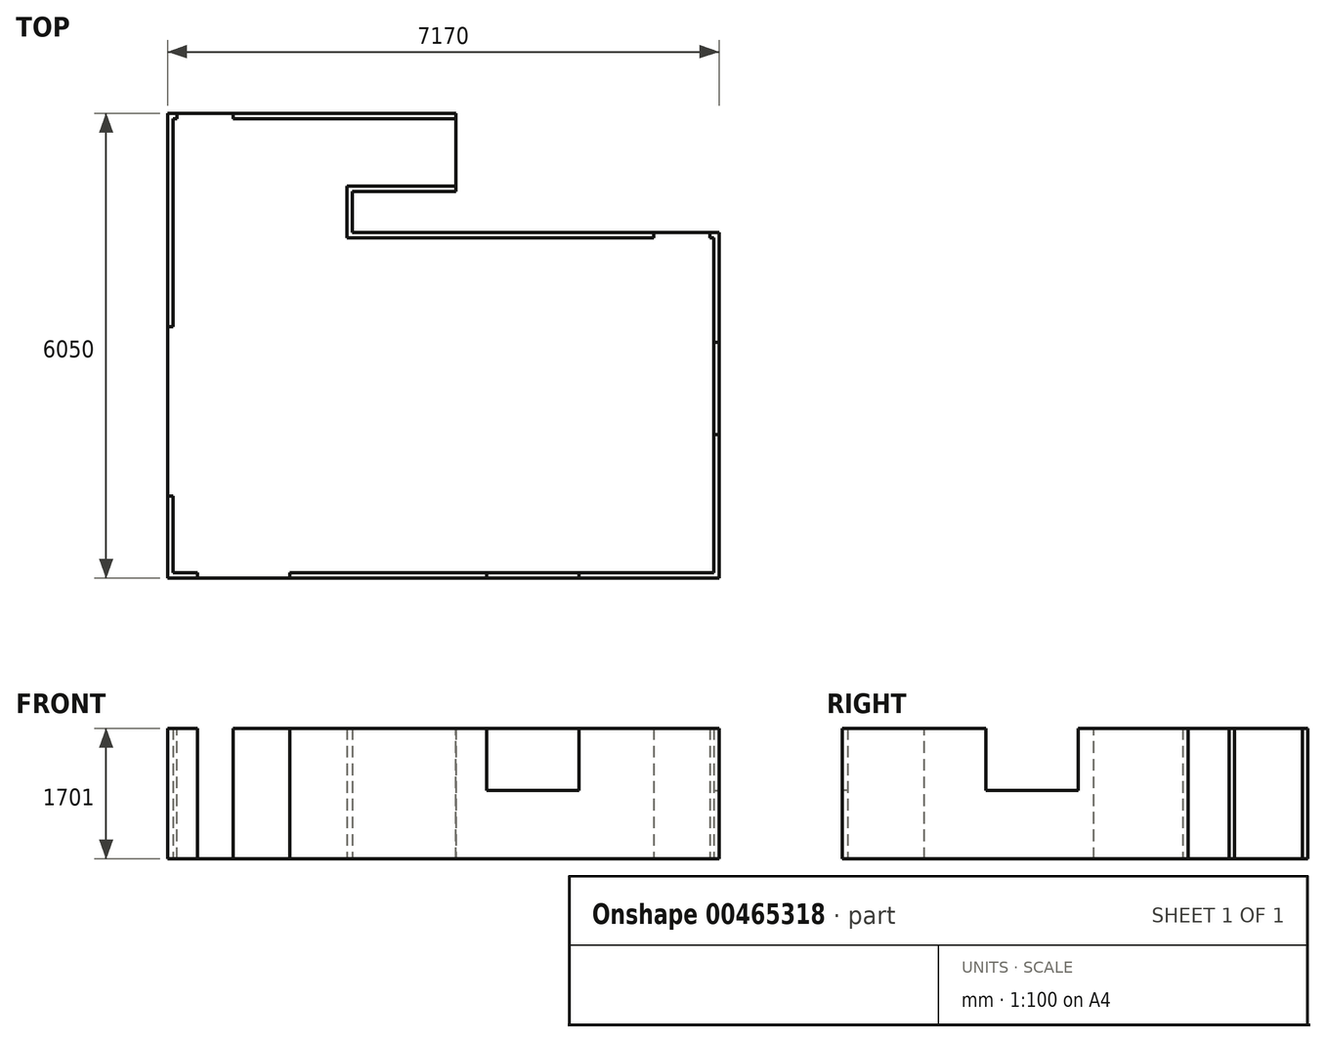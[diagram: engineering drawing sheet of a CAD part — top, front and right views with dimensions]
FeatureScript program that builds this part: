
annotation { "Feature Type Name" : "Feature", "Feature Type Description" : "" }
export const myFeature = defineFeature(function(context is Context, id is Id, definition is map)
    precondition{}
    {
        {
            var Q0;
            Q0=qCreatedBy(makeId("Top.planeOp"),FACE);
            var sketch = newSketch(context, id + "F0", { "sketchPlane" : qUnion([Q0])});
            skLineSegment(sketch, "E0", {"start": v(0, 0) * mm, "end": v(7030, 0) * mm});
            skLineSegment(sketch, "E1", {"start": v(7030, 0) * mm, "end": v(7030, 4360) * mm});
            skLineSegment(sketch, "E2", {"start": v(7030, 4360) * mm, "end": v(2260, 4360) * mm});
            skLineSegment(sketch, "E3", {"start": v(2260, 4360) * mm, "end": v(2260, 5030) * mm});
            skLineSegment(sketch, "E4", {"start": v(2260, 5030) * mm, "end": v(3610, 5030) * mm});
            skLineSegment(sketch, "E5", {"start": v(3610, 5030) * mm, "end": v(3610, 5910) * mm});
            skLineSegment(sketch, "E6", {"start": v(3610, 5910) * mm, "end": v(0, 5910) * mm});
            skLineSegment(sketch, "E7", {"start": v(0, 5910) * mm, "end": v(0, 0) * mm});
            skLineSegment(sketch, "E8.0", {"start": v(3680, 4960) * mm, "end": v(3680, 5980) * mm});
            skLineSegment(sketch, "E8.1", {"start": v(2330, 4960) * mm, "end": v(3680, 4960) * mm});
            skLineSegment(sketch, "E8.2", {"start": v(3680, 5980) * mm, "end": v(-70, 5980) * mm});
            skLineSegment(sketch, "E8.3", {"start": v(2330, 4430) * mm, "end": v(2330, 4960) * mm});
            skLineSegment(sketch, "E8.4", {"start": v(-70, 5980) * mm, "end": v(-70, -70) * mm});
            skLineSegment(sketch, "E8.5", {"start": v(-70, -70) * mm, "end": v(7100, -70) * mm});
            skLineSegment(sketch, "E8.6", {"start": v(7100, -70) * mm, "end": v(7100, 4430) * mm});
            skLineSegment(sketch, "E8.7", {"start": v(7100, 4430) * mm, "end": v(2330, 4430) * mm});
            skSolve(sketch);
        }
        {
            var Q0;
            Q0 = qSketchRegion(id + "F0", true);
            extrude(context, id + "F1", {"entities" : qUnion([Q0]), "depth" : 2700 * mm});
        }
        {
            var Q0;
            Q0=qCreatedBy(makeId("Top.planeOp"),FACE);
            var sketch = newSketch(context, id + "F2", { "sketchPlane" : qUnion([Q0])});
            skLineSegment(sketch, "E9.0", {"start": v(-70, 5980) * mm, "end": v(-70, -70) * mm});
            skLineSegment(sketch, "E9.1", {"start": v(3680, 5980) * mm, "end": v(-70, 5980) * mm});
            skLineSegment(sketch, "E9.2", {"start": v(3680, 4960) * mm, "end": v(3680, 5980) * mm});
            skLineSegment(sketch, "E9.3", {"start": v(2330, 4960) * mm, "end": v(3680, 4960) * mm});
            skLineSegment(sketch, "E9.4", {"start": v(2330, 4430) * mm, "end": v(2330, 4960) * mm});
            skLineSegment(sketch, "E9.5", {"start": v(7100, 4430) * mm, "end": v(2330, 4430) * mm});
            skLineSegment(sketch, "E9.6", {"start": v(7100, -70) * mm, "end": v(7100, 4430) * mm});
            skLineSegment(sketch, "E9.7", {"start": v(-70, -70) * mm, "end": v(7100, -70) * mm});
            skSolve(sketch);
        }
        {
            var Q0;
            Q0 = qSketchRegion(id + "F2", true);
            extrude(context, id + "F3", {"entities" : qUnion([Q0]), "operationType" : NewBodyOperationType.ADD, "oppositeDirection" : true, "depth" : 1 * mm});
        }
        {
            var Q0;
            Q0=makeQuery(id+"F3.boolean.opBoolean","MERGE",FACE,{"derivedFrom":[makeQuery(id+"F1.opExtrude","SWEPT_FACE",FACE,{"disambiguationData":[OSD([sQuery(id+"F0.wireOp",EDGE,"E8.5")])]}),makeQuery(id+"F3.opExtrude","SWEPT_FACE",FACE,{"disambiguationData":[OSD([sQuery(id+"F2.wireOp",EDGE,"E9.7")])]})]});
            var sketch = newSketch(context, id + "F4", { "sketchPlane" : qUnion([Q0])});
            skLineSegment(sketch, "E10.bottom", {"start": v(320, 0) * mm, "end": v(1520, 0) * mm});
            skLineSegment(sketch, "E10.top", {"start": v(320, 2320) * mm, "end": v(1520, 2320) * mm});
            skLineSegment(sketch, "E10.left", {"start": v(320, 0) * mm, "end": v(320, 2320) * mm});
            skLineSegment(sketch, "E10.right", {"start": v(1520, 0) * mm, "end": v(1520, 2320) * mm});
            skLineSegment(sketch, "E11.bottom", {"start": v(4080, 2290) * mm, "end": v(5280, 2290) * mm});
            skLineSegment(sketch, "E11.top", {"start": v(4080, 890) * mm, "end": v(5280, 890) * mm});
            skLineSegment(sketch, "E11.left", {"start": v(4080, 2290) * mm, "end": v(4080, 890) * mm});
            skLineSegment(sketch, "E11.right", {"start": v(5280, 2290) * mm, "end": v(5280, 890) * mm});
            skSolve(sketch);
        }
        {
            var Q0;
            Q0 = qSketchRegion(id + "F4", true);
            extrude(context, id + "F5", {"entities" : qUnion([Q0]), "operationType" : NewBodyOperationType.REMOVE, "oppositeDirection" : true, "depth" : 70 * mm});
        }
        {
            var Q0;
            Q0=makeQuery(id+"F3.boolean.opBoolean","MERGE",FACE,{"derivedFrom":[makeQuery(id+"F1.opExtrude","SWEPT_FACE",FACE,{"disambiguationData":[OSD([sQuery(id+"F0.wireOp",EDGE,"E8.6")])]}),makeQuery(id+"F3.opExtrude","SWEPT_FACE",FACE,{"disambiguationData":[OSD([sQuery(id+"F2.wireOp",EDGE,"E9.6")])]})]});
            var sketch = newSketch(context, id + "F6", { "sketchPlane" : qUnion([Q0])});
            skLineSegment(sketch, "E12.bottom", {"start": v(1800, 2290) * mm, "end": v(3000, 2290) * mm});
            skLineSegment(sketch, "E12.top", {"start": v(1800, 890) * mm, "end": v(3000, 890) * mm});
            skLineSegment(sketch, "E12.left", {"start": v(1800, 2290) * mm, "end": v(1800, 890) * mm});
            skLineSegment(sketch, "E12.right", {"start": v(3000, 2290) * mm, "end": v(3000, 890) * mm});
            skSolve(sketch);
        }
        {
            var Q0;
            Q0 = qSketchRegion(id + "F6", true);
            extrude(context, id + "F7", {"entities" : qUnion([Q0]), "operationType" : NewBodyOperationType.REMOVE, "oppositeDirection" : true, "depth" : 70 * mm});
        }
        {
            var Q0;
            Q0=makeQuery(id+"F3.boolean.opBoolean","MERGE",FACE,{"derivedFrom":[makeQuery(id+"F1.opExtrude","SWEPT_FACE",FACE,{"disambiguationData":[OSD([sQuery(id+"F0.wireOp",EDGE,"E8.4")])]}),makeQuery(id+"F3.opExtrude","SWEPT_FACE",FACE,{"disambiguationData":[OSD([sQuery(id+"F2.wireOp",EDGE,"E9.0")])]})]});
            var sketch = newSketch(context, id + "F8", { "sketchPlane" : qUnion([Q0])});
            skLineSegment(sketch, "E13.bottom", {"start": v(-3200, 0) * mm, "end": v(-1000, 0) * mm});
            skLineSegment(sketch, "E13.top", {"start": v(-3200, 2100) * mm, "end": v(-1000, 2100) * mm});
            skLineSegment(sketch, "E13.left", {"start": v(-3200, 0) * mm, "end": v(-3200, 2100) * mm});
            skLineSegment(sketch, "E13.right", {"start": v(-1000, 0) * mm, "end": v(-1000, 2100) * mm});
            skSolve(sketch);
        }
        {
            var Q0;
            Q0 = qSketchRegion(id + "F8", true);
            extrude(context, id + "F9", {"entities" : qUnion([Q0]), "operationType" : NewBodyOperationType.REMOVE, "oppositeDirection" : true, "depth" : 70 * mm});
        }
        {
            var Q0;
            Q0=makeQuery(id+"F1.opExtrude","SWEPT_FACE",FACE,{"disambiguationData":[OSD([sQuery(id+"F0.wireOp",EDGE,"E2")])]});
            var sketch = newSketch(context, id + "F10", { "sketchPlane" : qUnion([Q0])});
            skLineSegment(sketch, "E14.bottom", {"start": v(6250, 2040) * mm, "end": v(6980, 2040) * mm});
            skLineSegment(sketch, "E14.top", {"start": v(6250, 0) * mm, "end": v(6980, 0) * mm});
            skLineSegment(sketch, "E14.left", {"start": v(6250, 2040) * mm, "end": v(6250, 0) * mm});
            skLineSegment(sketch, "E14.right", {"start": v(6980, 2040) * mm, "end": v(6980, 0) * mm});
            skLineSegment(sketch, "E15.bottom", {"start": v(50, 2040) * mm, "end": v(780, 2040) * mm});
            skLineSegment(sketch, "E15.top", {"start": v(50, 0) * mm, "end": v(780, 0) * mm});
            skLineSegment(sketch, "E15.left", {"start": v(50, 2040) * mm, "end": v(50, 0) * mm});
            skLineSegment(sketch, "E15.right", {"start": v(780, 2040) * mm, "end": v(780, 0) * mm});
            skSolve(sketch);
        }
        {
            var Q0;
            Q0 = qSketchRegion(id + "F10", true);
            var Q1;
            Q1=makeQuery(id+"F3.boolean.opBoolean","MERGE",FACE,{"derivedFrom":[makeQuery(id+"F1.opExtrude","SWEPT_FACE",FACE,{"disambiguationData":[OSD([sQuery(id+"F0.wireOp",EDGE,"E8.2")])]}),makeQuery(id+"F3.opExtrude","SWEPT_FACE",FACE,{"disambiguationData":[OSD([sQuery(id+"F2.wireOp",EDGE,"E9.1")])]})]});
            extrude(context, id + "F11", {"entities" : qUnion([Q0]), "operationType" : NewBodyOperationType.REMOVE, "endBound" : BoundingType.UP_TO_SURFACE, "oppositeDirection" : true, "endBoundEntityFace" : qUnion([Q1]), "depth" : 25 * mm});
        }
        {
            var Q0;
            Q0=makeQuery(id+"F1.opExtrude","CAP_FACE",FACE,{"disambiguationData":[OSD([sQuery(id+"F0.wireOp",EDGE,"E0"),sQuery(id+"F0.wireOp",EDGE,"E1"),sQuery(id+"F0.wireOp",EDGE,"E2"),sQuery(id+"F0.wireOp",EDGE,"E3"),sQuery(id+"F0.wireOp",EDGE,"E4"),sQuery(id+"F0.wireOp",EDGE,"E5"),sQuery(id+"F0.wireOp",EDGE,"E6"),sQuery(id+"F0.wireOp",EDGE,"E7"),sQuery(id+"F0.wireOp",EDGE,"E8.0"),sQuery(id+"F0.wireOp",EDGE,"E8.1"),sQuery(id+"F0.wireOp",EDGE,"E8.2"),sQuery(id+"F0.wireOp",EDGE,"E8.3"),sQuery(id+"F0.wireOp",EDGE,"E8.4"),sQuery(id+"F0.wireOp",EDGE,"E8.5"),sQuery(id+"F0.wireOp",EDGE,"E8.6"),sQuery(id+"F0.wireOp",EDGE,"E8.7")])],"isStart":false});
            var sketch = newSketch(context, id + "F12", { "sketchPlane" : qUnion([Q0])});
            skLineSegment(sketch, "E16.bottom", {"start": v(3610, 5910) * mm, "end": v(3680, 5910) * mm});
            skLineSegment(sketch, "E16.top", {"start": v(3610, 5030) * mm, "end": v(3680, 5030) * mm});
            skLineSegment(sketch, "E16.left", {"start": v(3610, 5910) * mm, "end": v(3610, 5030) * mm});
            skLineSegment(sketch, "E16.right", {"start": v(3680, 5910) * mm, "end": v(3680, 5030) * mm});
            skSolve(sketch);
        }
        {
            var Q0;
            Q0 = qSketchRegion(id + "F12", true);
            var Q1;
            Q1=makeQuery(id+"F11.boolean.opBoolean","MERGE",FACE,{"derivedFrom":[makeQuery(id+"F9.boolean.opBoolean","MERGE",FACE,{"derivedFrom":[makeQuery(id+"F5.boolean.opBoolean","MERGE",FACE,{"derivedFrom":[makeQuery(id+"F3.opExtrude","CAP_FACE",FACE,{"disambiguationData":[OSD([sQuery(id+"F2.wireOp",EDGE,"E9.0"),sQuery(id+"F2.wireOp",EDGE,"E9.1"),sQuery(id+"F2.wireOp",EDGE,"E9.2"),sQuery(id+"F2.wireOp",EDGE,"E9.3"),sQuery(id+"F2.wireOp",EDGE,"E9.4"),sQuery(id+"F2.wireOp",EDGE,"E9.5"),sQuery(id+"F2.wireOp",EDGE,"E9.6"),sQuery(id+"F2.wireOp",EDGE,"E9.7")])],"isStart":true}),makeQuery(id+"F5.opExtrude","SWEPT_FACE",FACE,{"disambiguationData":[OSD([sQuery(id+"F4.wireOp",EDGE,"E10.bottom")])]})]}),makeQuery(id+"F9.opExtrude","SWEPT_FACE",FACE,{"disambiguationData":[OSD([sQuery(id+"F8.wireOp",EDGE,"E13.bottom")])]})]}),makeQuery(id+"F11.opExtrude","SWEPT_FACE",FACE,{"disambiguationData":[OSD([sQuery(id+"F10.wireOp",EDGE,"E14.top")])]}),makeQuery(id+"F11.opExtrude","SWEPT_FACE",FACE,{"disambiguationData":[OSD([sQuery(id+"F10.wireOp",EDGE,"E15.top")])]})]});
            extrude(context, id + "F13", {"entities" : qUnion([Q0]), "operationType" : NewBodyOperationType.REMOVE, "endBound" : BoundingType.UP_TO_SURFACE, "oppositeDirection" : true, "endBoundEntityFace" : qUnion([Q1]), "depth" : 25 * mm});
        }
        {
            var Q0;
            Q0=makeQuery(id+"F1.opExtrude","CAP_FACE",FACE,{"disambiguationData":[OSD([sQuery(id+"F0.wireOp",EDGE,"E0"),sQuery(id+"F0.wireOp",EDGE,"E1"),sQuery(id+"F0.wireOp",EDGE,"E2"),sQuery(id+"F0.wireOp",EDGE,"E3"),sQuery(id+"F0.wireOp",EDGE,"E4"),sQuery(id+"F0.wireOp",EDGE,"E5"),sQuery(id+"F0.wireOp",EDGE,"E6"),sQuery(id+"F0.wireOp",EDGE,"E7"),sQuery(id+"F0.wireOp",EDGE,"E8.0"),sQuery(id+"F0.wireOp",EDGE,"E8.1"),sQuery(id+"F0.wireOp",EDGE,"E8.2"),sQuery(id+"F0.wireOp",EDGE,"E8.3"),sQuery(id+"F0.wireOp",EDGE,"E8.4"),sQuery(id+"F0.wireOp",EDGE,"E8.5"),sQuery(id+"F0.wireOp",EDGE,"E8.6"),sQuery(id+"F0.wireOp",EDGE,"E8.7")])],"isStart":false});
            var sketch = newSketch(context, id + "F14", { "sketchPlane" : qUnion([Q0])});
            skLineSegment(sketch, "E17.0", {"start": v(-70, -70) * mm, "end": v(7100, -70) * mm});
            skLineSegment(sketch, "E17.1", {"start": v(7100, -70) * mm, "end": v(7100, 4430) * mm});
            skLineSegment(sketch, "E17.2", {"start": v(-70, 5980) * mm, "end": v(-70, -70) * mm});
            skLineSegment(sketch, "E17.3", {"start": v(3680, 5980) * mm, "end": v(-70, 5980) * mm});
            skLineSegment(sketch, "E18", {"start": v(3680, 5980) * mm, "end": v(7100, 4430) * mm});
            skSolve(sketch);
        }
        {
            var Q0;
            Q0 = qSketchRegion(id + "F14", true);
            extrude(context, id + "F15", {"entities" : qUnion([Q0]), "operationType" : NewBodyOperationType.REMOVE, "oppositeDirection" : true, "depth" : 1000 * mm});
        }
    });
